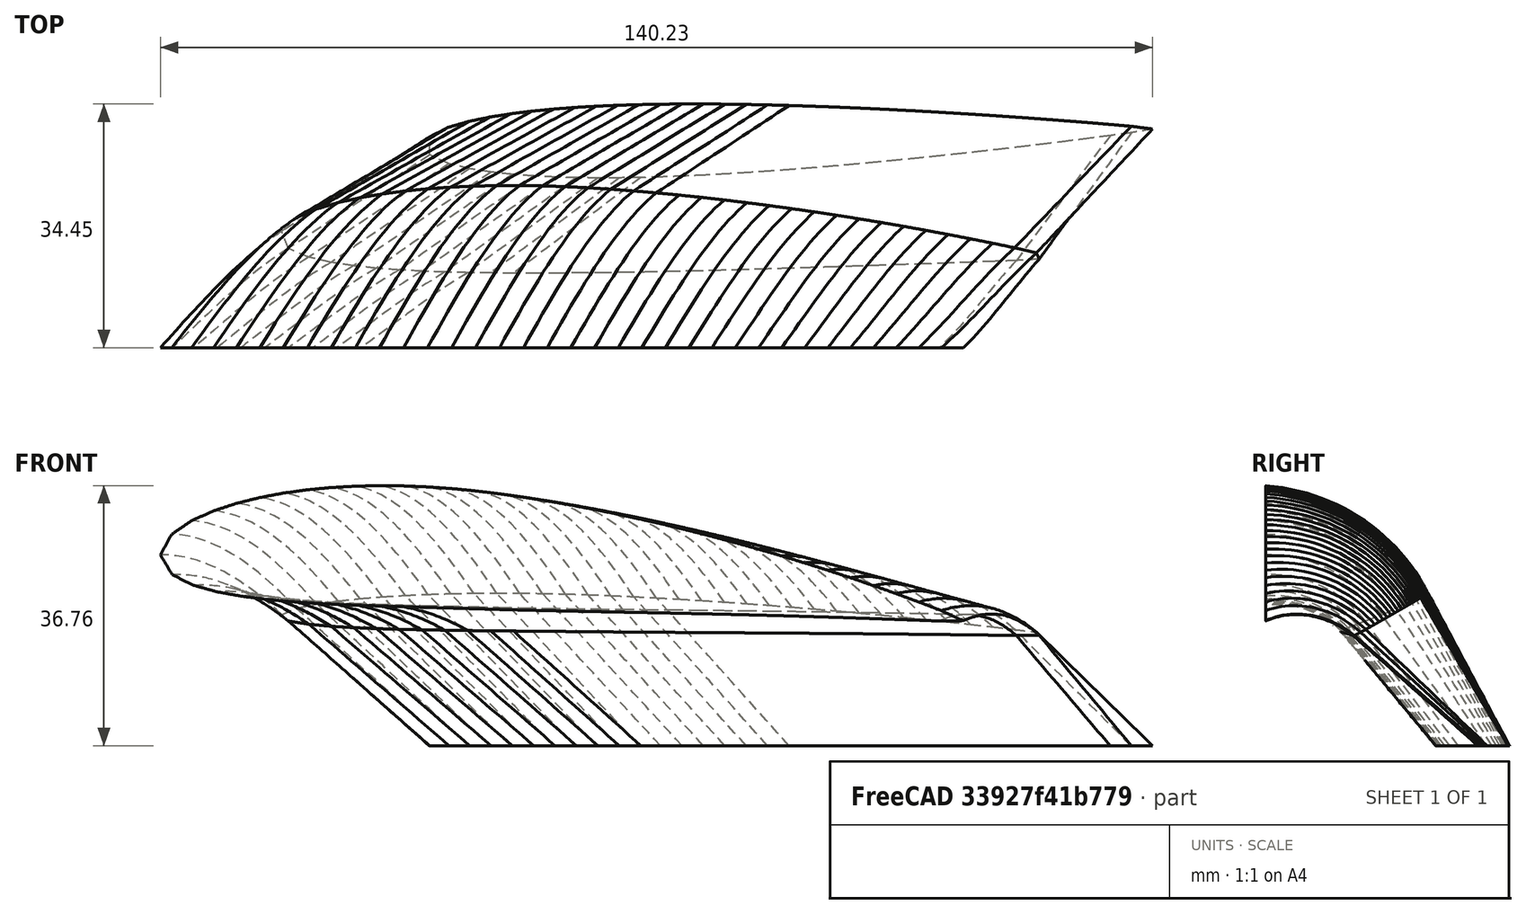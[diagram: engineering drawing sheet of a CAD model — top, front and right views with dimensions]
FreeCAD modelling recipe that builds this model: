
FCSTD DOCUMENT  (FreeCAD 1.0R39319 (Git))
Label: Winglet
License: All rights reserved
LicenseURL: https://en.wikipedia.org/wiki/All_rights_reserved
objects: Part::FeaturePython×4, App::DocumentObjectGroup×3, PartDesign::SubShapeBinder×3, Part::Part2DObjectPython×2, Sketcher::SketchObject×1, Part::Sweep×1, App::Part×1
note: 12 computed .brp shape members not serialized (recipe doc carries the construction recipe); baked Part::Feature solids carry a one-line shape summary decoded from their .brp
EXTERNAL_REF file=Spreadsheet.FCStd obj=plane

FEATURE [Part::Part2DObjectPython] Wire  # Draft 2D object (typed FeaturePython)
  Area = 0.0682453
  ChamferSize = 0
  Closed = true
  End = (0.970786,-0.004405,0)
  FilletRadius = 0
  Length = 2.02397
  MakeFace = true
  Points = (69) [(1,0,0),(0.970786,0.004405,0),(0.941558,0.007646,0),(0.912319,0.010777,0),(0.883069,0.013804,0),(0.853809,0.016731,0),(0.824539,0.019561,0),+62 more]
  Start = (1,0,0)
  Subdivisions = 0
FEATURE [App::DocumentObjectGroup] naca0010
  Group = -> [Wire]
FEATURE [Part::Part2DObjectPython] Wire001  # Draft 2D object (typed FeaturePython)
  Area = 0.102817
  ChamferSize = 0
  Closed = true
  End = (0.969889,-0.002758,0)
  FilletRadius = 0
  Length = 2.06327
  MakeFace = true
  Points = (69) [(1,0,0),(0.971604,0.010359,0),(0.942895,0.018808,0),(0.914088,0.026914,0),(0.885187,0.034682,0),(0.856199,0.042118,0),(0.827128,0.049224,0),+62 more]
  Start = (1,0,0)
  Subdivisions = 0
FEATURE [App::DocumentObjectGroup] naca4415
  Group = -> [Wire001]
FEATURE [App::DocumentObjectGroup] Group  label="Airfoils Low Poly"
  Group = -> [naca0010,naca4415]
FEATURE [PartDesign::SubShapeBinder] Binder  label="Wing Tip"
  BindCopyOnChange = 0
  BindMode = 0
  ClaimChildren = false
  Context = -> Part [Binder.]
  Fuse = false
  MakeFace = true
  OffsetFill = false
  OffsetIntersection = false
  OffsetJoinType = 0
  OffsetOpenResult = false
  PartialLoad = false
  Placement = pos=(0,0,0) rot=(1,0,0;1.5708rad)
  Refine = true
  Relative = true
  Support = -> [naca4415]
  _Version = 2
FEATURE [PartDesign::SubShapeBinder] Binder001  label="Winglet Tip"
  BindCopyOnChange = 0
  BindMode = 0
  ClaimChildren = false
  Context = -> Part [Binder001.]
  Fuse = false
  MakeFace = true
  OffsetFill = false
  OffsetIntersection = false
  OffsetJoinType = 0
  OffsetOpenResult = false
  PartialLoad = false
  Placement = pos=(0,0,0) rot=(1,0,0;1.5708rad)
  Refine = true
  Relative = true
  Support = -> [Wire]
  _Version = 2
FEATURE [PartDesign::SubShapeBinder] Binder002  label="Winglet Curve End"
  BindCopyOnChange = 0
  BindMode = 0
  ClaimChildren = false
  Context = -> Part [Binder002.]
  Fuse = false
  MakeFace = true
  OffsetFill = false
  OffsetIntersection = false
  OffsetJoinType = 0
  OffsetOpenResult = false
  PartialLoad = false
  Placement = pos=(0,0,0) rot=(1,0,0;1.5708rad)
  Refine = true
  Relative = true
  Support = -> [Wire]
  _Version = 2
FEATURE [Part::FeaturePython] Clone  label="Wing Tip001"  # Draft clone (typed FeaturePython)
  AttacherType = Attacher::AttachEngine3D
  AttachmentOffset = pos=(275.624,1.47756,-508.507) rot=(0,0,1;-0.078559rad)
  AttachmentSupport = -> [XZ_Plane]
  Fuse = false
  MapMode = 5
  Objects = -> [Binder]
  Placement = pos=(275.624,508.507,1.47756) rot=(-0.998459,-0.039239,0.039239;4.71085rad)
  Scale = (113.823,113.823,1)
  expr: .AttachmentOffset.Base.x = <<Spreadsheet>>#plane.body_len * <<Spreadsheet>>#plane.wing_base_start * 1000 + sin(<<Spreadsheet>>#plane.sweep) * <<Spreadsheet>>#plane.leading_edge_length * 1000
  expr: .AttachmentOffset.Base.y = sin(Spreadsheet#plane.dihedral) * Spreadsheet#plane.leading_edge_length * 1000
  expr: .AttachmentOffset.Base.z = -(Spreadsheet#plane.body_span * 1000 + cos(Spreadsheet#plane.sweep) * cos(Spreadsheet#plane.dihedral) * Spreadsheet#plane.leading_edge_length * 1000)
  expr: .AttachmentOffset.Rotation.Angle = -Spreadsheet#plane.attack_angle - Spreadsheet#plane.washout
  expr: .Scale.x = <<Spreadsheet>>#plane.wing_chord * 1000 * <<Spreadsheet>>#plane.taper_ratio
  expr: .Scale.y = <<Spreadsheet>>#plane.wing_chord * <<Spreadsheet>>#plane.taper_ratio * <<Spreadsheet>>#plane.scale_y_wing_tip * 1000
FEATURE [Part::FeaturePython] Clone002  label="Winglet Tip003"  # Draft clone (typed FeaturePython)
  AttacherType = Attacher::AttachEngine3D
  AttachmentOffset = pos=(312.874,-25.1291,-537.009) rot=(1,0,0;1.5708rad)
  AttachmentSupport = -> [XZ_Plane]
  Fuse = false
  MapMode = 5
  Objects = -> [Binder001]
  Placement = pos=(312.874,537.009,-25.1291) rot=(1,0,0;3.14159rad)
  Scale = (102.999,102.999,1)
  expr: .AttachmentOffset.Base.x = -sin(Spreadsheet#plane.winglet_angle) * Spreadsheet#plane.winglet_radius * 1000 * tan(Spreadsheet#plane.winglet_sweep) + sin(Spreadsheet#plane.winglet_sweep) * Spreadsheet#plane.winglet_leading_edge_len * 1000 + Spreadsheet#plane.body_len * Spreadsheet#plane.wing_base_start * 1000 + sin(Spreadsheet#plane.sweep) * Spreadsheet#plane.leading_edge_length * 1000
  expr: .AttachmentOffset.Base.y = -1 * ((1 - cos(Spreadsheet#plane.winglet_angle)) * Spreadsheet#plane.winglet_radius * 1000 - sin(Spreadsheet#plane.winglet_angle) * cos(Spreadsheet#plane.winglet_sweep) * Spreadsheet#plane.winglet_leading_edge_len * 1000) + sin(Spreadsheet#plane.dihedral) * Spreadsheet#plane.leading_edge_length * 1000
  expr: .AttachmentOffset.Base.z = sin(Spreadsheet#plane.winglet_angle) * Spreadsheet#plane.winglet_radius * 1000 - cos(Spreadsheet#plane.winglet_angle) * cos(Spreadsheet#plane.winglet_sweep) * Spreadsheet#plane.winglet_leading_edge_len * 1000 - (Spreadsheet#plane.body_span * 1000 + cos(Spreadsheet#plane.sweep) * cos(Spreadsheet#plane.dihedral) * Spreadsheet#plane.leading_edge_length * 1000)
  expr: .AttachmentOffset.Rotation.Angle = 90
  expr: .Scale.x = Spreadsheet#plane.wing_chord * Spreadsheet#plane.taper_ratio * Spreadsheet#plane.winglet_taper_ratio * 1000
  expr: .Scale.y = Spreadsheet#plane.wing_chord * Spreadsheet#plane.taper_ratio * Spreadsheet#plane.winglet_taper_ratio * 1000
FEATURE [Sketcher::SketchObject] Sketch
  ArcFitTolerance = 1e-06
  AttachmentOffset = pos=(508.507,1.47756,275.624) rot=(0,1,0;0rad)
  AttachmentSupport = -> [YZ_Plane]
  FullyConstrained = true
  MakeInternals = false
  MapMode = 5
  Placement = pos=(275.624,508.507,1.47756) rot=(0.57735,0.57735,0.57735;2.0944rad)
  expr: .AttachmentOffset.Base.x = Spreadsheet#plane.body_span * 1000 + cos(Spreadsheet#plane.sweep) * cos(Spreadsheet#plane.dihedral) * Spreadsheet#plane.leading_edge_length * 1000
  expr: .AttachmentOffset.Base.y = sin(Spreadsheet#plane.dihedral) * Spreadsheet#plane.leading_edge_length * 1000
  expr: .AttachmentOffset.Base.z = <<Spreadsheet>>#plane.body_len * <<Spreadsheet>>#plane.wing_base_start * 1000 + sin(<<Spreadsheet>>#plane.sweep) * <<Spreadsheet>>#plane.leading_edge_length * 1000
  expr: .AttachmentOffset.Rotation.Angle = 0
  expr: Constraints[2] = Spreadsheet#plane.winglet_radius * 1000
  expr: Constraints[3] = -Spreadsheet#plane.winglet_angle
  expr: Constraints[5] = Spreadsheet#plane.winglet_angle + 90
  expr: Constraints[6] = Spreadsheet#plane.winglet_leading_edge_len * 1000 * cos(Spreadsheet#plane.winglet_sweep)
  sketch-geometry (2):
    g0: ArcOfCircle CenterX=0 CenterY=-19.1236 CenterZ=0 NormalX=0 NormalY=0 NormalZ=1 AngleXU=0 Radius=19.1236 StartAngle=0.607806 EndAngle=1.5708
    g1: LineSegment StartX=15.6986 StartY=-8.20274 StartZ=0 EndX=28.5015 EndY=-26.6067 EndZ=0
  constraints (7):
    c: PointOnObject(g0,g-2)
    c: Coincident(g0,g-1)
    c: Radius(g0) = 19.1236
    c: Angle(g0) = 0.96299
    c: Coincident(g1,g0)
    c: Angle(g-2,g1) = 0.607806
    c: Distance(g1,g1) = 22.4191
FEATURE [Part::FeaturePython] Clone003  label="Winglet Tip Toed neg"  # Draft clone (typed FeaturePython)
  AttacherType = Attacher::AttachEngine3D
  AttachmentOffset = pos=(0,0,0) rot=(0,0,1;0.023489rad)
  AttachmentSupport = -> [Clone002]
  Fuse = false
  MapMode = 2
  Objects = -> [Clone002]
  Placement = pos=(312.874,537.009,-25.1291) rot=(0.999931,-0.011744,0;3.14159rad)
  Scale = (1,1,1)
  expr: .AttachmentOffset.Base.x = 0
  expr: .AttachmentOffset.Base.y = 0
  expr: .AttachmentOffset.Base.z = 0
  expr: .AttachmentOffset.Rotation.Angle = -Spreadsheet#plane.winglet_toe
  expr: .AttachmentOffset.Rotation.Yaw = Spreadsheet#plane.winglet_toe
  expr: .Placement.Rotation.Yaw = Spreadsheet#plane.winglet_toe
FEATURE [Part::FeaturePython] Clone004  label="Winglet Tip Toed"  # Draft clone (typed FeaturePython)
  AttacherType = Attacher::AttachEngine3D
  AttachmentOffset = pos=(0,0,0) rot=(0,0,-1;0.023489rad)
  AttachmentSupport = -> [Clone002]
  Fuse = false
  MapMode = 2
  Objects = -> [Clone002]
  Placement = pos=(312.874,537.009,-25.1291) rot=(0.999931,0.011744,0;3.14159rad)
  Scale = (1,1,1)
  expr: .AttachmentOffset.Rotation.Angle = Spreadsheet#plane.winglet_toe
FEATURE [Part::Sweep] Sweep
  Frenet = true
  Sections = -> [Clone,Clone004]
  Solid = true
  Spine = -> Sketch [Edge2,Edge1]
  Transition = 1
FEATURE [App::Part] Part
  Group = -> [Group,Wire,naca0010,Wire001,naca4415,Binder002,Binder001,Binder,Clone,Clone002,Sketch,Clone003,Clone004,Sweep]
  Origin = -> Origin
